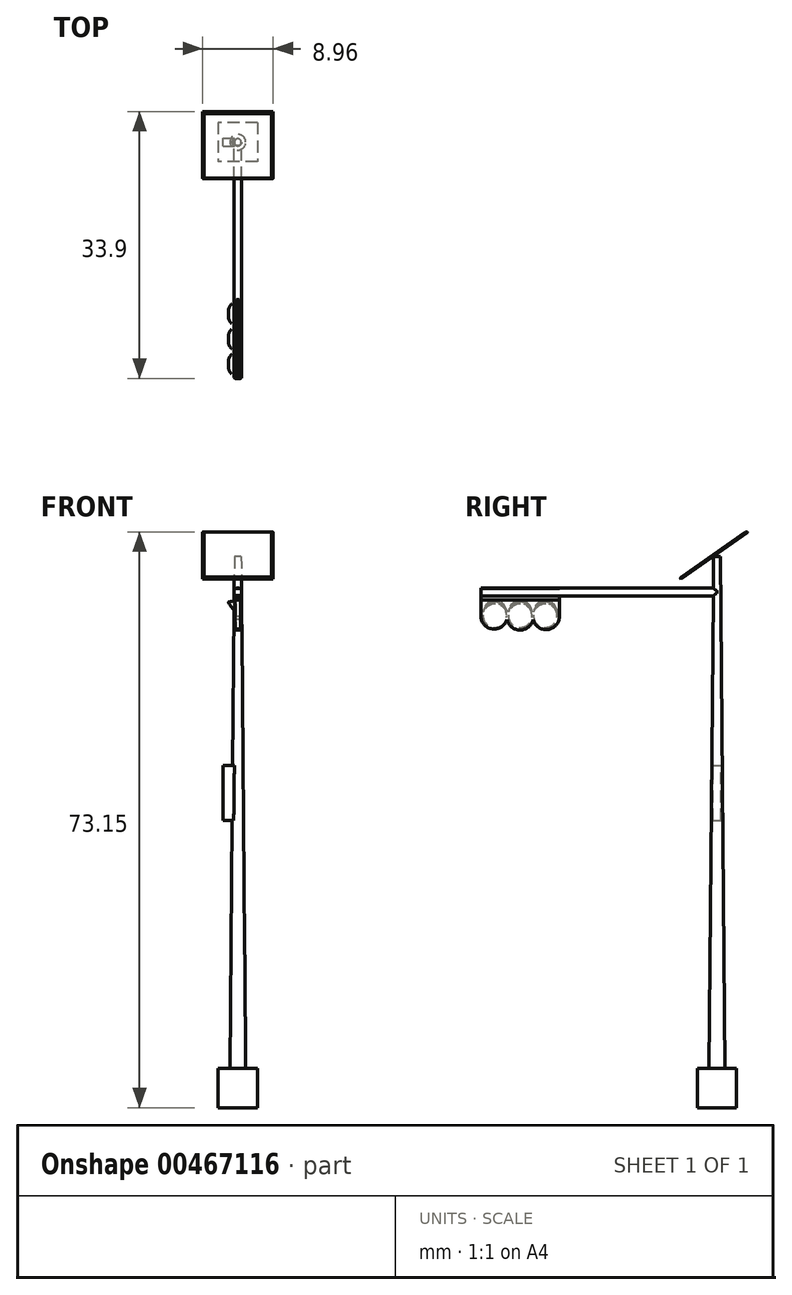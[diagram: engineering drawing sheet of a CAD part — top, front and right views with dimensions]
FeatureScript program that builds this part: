
annotation { "Feature Type Name" : "Feature", "Feature Type Description" : "" }
export const myFeature = defineFeature(function(context is Context, id is Id, definition is map)
    precondition{}
    {
        {
            var Q0;
            Q0=qCreatedBy(makeId("Top.planeOp"),FACE);
            var sketch = newSketch(context, id + "F0", { "sketchPlane" : qUnion([Q0])});
            skLineSegment(sketch, "E0.bottom", {"start": v(2.5, 2.5) * mm, "end": v(-2.5, 2.5) * mm});
            skLineSegment(sketch, "E0.top", {"start": v(2.5, -2.5) * mm, "end": v(-2.5, -2.5) * mm});
            skLineSegment(sketch, "E0.left", {"start": v(2.5, 2.5) * mm, "end": v(2.5, -2.5) * mm});
            skLineSegment(sketch, "E0.right", {"start": v(-2.5, 2.5) * mm, "end": v(-2.5, -2.5) * mm});
            skPoint(sketch, "E0.middle", {"position": v(0, 0) * mm});
            skSolve(sketch);
        }
        {
            var Q0;
            Q0 = qSketchRegion(id + "F0", true);
            extrude(context, id + "F1", {"entities" : qUnion([Q0]), "depth" : 5 * mm});
        }
        {
            var Q0;
            Q0=makeQuery(id+"F1.opExtrude","CAP_FACE",FACE,{"disambiguationData":[OSD([sQuery(id+"F0.wireOp",EDGE,"E0.bottom"),sQuery(id+"F0.wireOp",EDGE,"E0.top"),sQuery(id+"F0.wireOp",EDGE,"E0.left"),sQuery(id+"F0.wireOp",EDGE,"E0.right")])],"isStart":false});
            var sketch = newSketch(context, id + "F2", { "sketchPlane" : qUnion([Q0])});
            skCircle(sketch, "E1", {"center": v(0, 0) * mm, "radius": 1 * mm});
            skSolve(sketch);
        }
        {
            var Q0;
            Q0 = qSketchRegion(id + "F2", true);
            extrude(context, id + "F3", {"entities" : qUnion([Q0]), "operationType" : NewBodyOperationType.ADD, "depth" : 65 * mm, "hasDraft" : true, "draftAngle" : 0.5 * degree, "draftPullDirection" : true});
        }
        {
            var Q0;
            Q0=makeQuery(id+"F1.opExtrude","SWEPT_FACE",FACE,{"disambiguationData":[OSD([sQuery(id+"F0.wireOp",EDGE,"E0.left")])]});
            cPlane(context, id + "F4", {"entities" : qUnion([Q0]), "cplaneType" : CPlaneType.OFFSET, "offset" : 2.5 * mm, "oppositeDirection" : true, "width" : 150 * mm, "height" : 150 * mm});
        }
        {
            var Q0;
            Q0=qCreatedBy(id+"F4.planeOp",FACE);
            var sketch = newSketch(context, id + "F5", { "sketchPlane" : qUnion([Q0])});
            skLineSegment(sketch, "E2", {"start": v(-3.33, 68) * mm, "end": v(2.66, 72.2) * mm, "construction": true});
            skLineSegment(sketch, "E3.0", {"start": v(-0.43, 70) * mm, "end": v(0.43, 70) * mm, "construction": true});
            skSolve(sketch);
        }
        {
            var Q0;
            Q0=sQuery(id+"F5.wireOp",EDGE,"E2");
            cPlane(context, id + "F6", {"entities" : qUnion([Q0]), "cplaneType" : CPlaneType.LINE_ANGLE, "offset" : 25 * mm, "angle" : 0 * degree, "width" : 150 * mm, "height" : 150 * mm});
        }
        {
            var Q0;
            Q0=makeQuery(id+"F1.opExtrude","SWEPT_FACE",FACE,{"disambiguationData":[OSD([sQuery(id+"F0.wireOp",EDGE,"E0.top")])]});
            cPlane(context, id + "F7", {"entities" : qUnion([Q0]), "cplaneType" : CPlaneType.OFFSET, "offset" : 2.5 * mm, "oppositeDirection" : true, "width" : 150 * mm, "height" : 150 * mm});
        }
        {
            var Q0;
            Q0=qCreatedBy(id+"F7.planeOp",FACE);
            var sketch = newSketch(context, id + "F8", { "sketchPlane" : qUnion([Q0])});
            skLineSegment(sketch, "E4.0", {"start": v(0, 65) * mm, "end": v(0, 72.2) * mm, "construction": true});
            skCircle(sketch, "E5", {"center": v(0, 65.5) * mm, "radius": 0.5 * mm});
            skSolve(sketch);
        }
        {
            var Q0;
            Q0 = qSketchRegion(id + "F8", true);
            extrude(context, id + "F9", {"entities" : qUnion([Q0]), "operationType" : NewBodyOperationType.ADD, "depth" : 30 * mm});
        }
        {
            var Q0;
            Q0=qCreatedBy(id+"F6.planeOp",FACE);
            var sketch = newSketch(context, id + "F10", { "sketchPlane" : qUnion([Q0])});
            skLineSegment(sketch, "E6.0", {"start": v(0, 36.27) * mm, "end": v(0, 43.59) * mm, "construction": true});
            skLineSegment(sketch, "E7.bottom", {"start": v(4.48, 34.76) * mm, "end": v(-4.48, 34.76) * mm});
            skLineSegment(sketch, "E7.top", {"start": v(4.48, 45.1) * mm, "end": v(-4.48, 45.1) * mm});
            skLineSegment(sketch, "E7.left", {"start": v(4.48, 34.76) * mm, "end": v(4.48, 45.1) * mm});
            skLineSegment(sketch, "E7.right", {"start": v(-4.48, 34.76) * mm, "end": v(-4.48, 45.1) * mm});
            skPoint(sketch, "E7.middle", {"position": v(0, 39.93) * mm});
            skSolve(sketch);
        }
        {
            var Q0;
            Q0 = qSketchRegion(id + "F10", true);
            extrude(context, id + "F11", {"entities" : qUnion([Q0]), "depth" : .2 * mm});
        }
        {
            var Q0;
            Q0=makeQuery(id+"F11.opExtrude","CAP_FACE",FACE,{"disambiguationData":[OSD([sQuery(id+"F10.wireOp",EDGE,"E7.bottom"),sQuery(id+"F10.wireOp",EDGE,"E7.top"),sQuery(id+"F10.wireOp",EDGE,"E7.left"),sQuery(id+"F10.wireOp",EDGE,"E7.right")])],"isStart":false});
            fillet(context, id + "F12", {"entities" : qUnion([Q0]), "radius" : .2 * mm, "tangentPropagation" : true, "allowEdgeOverflow" : false});
        }
        {
            var Q0;
            Q0=qCreatedBy(id+"F4.planeOp",FACE);
            var sketch = newSketch(context, id + "F13", { "sketchPlane" : qUnion([Q0])});
            skLineSegment(sketch, "E8", {"start": v(-0.48, 65) * mm, "end": v(-20, 65) * mm, "construction": true});
            skLineSegment(sketch, "E9", {"start": v(-1, 5) * mm, "end": v(-0.43, 70) * mm, "construction": true});
            skLineSegment(sketch, "E10.top", {"start": v(-30, 64.5) * mm, "end": v(-20, 64.5) * mm});
            skLineSegment(sketch, "E10.left", {"start": v(-30, 66) * mm, "end": v(-30, 64.5) * mm});
            skLineSegment(sketch, "E10.right", {"start": v(-20, 66) * mm, "end": v(-20, 64.5) * mm});
            skLineSegment(sketch, "E11", {"start": v(-30, 66) * mm, "end": v(-0.47, 66) * mm});
            skLineSegment(sketch, "E12.0", {"start": v(-30, 65) * mm, "end": v(-30, 66) * mm});
            skSolve(sketch);
        }
        {
            var Q0;
            Q0 = qSketchRegion(id + "F13", true);
            extrude(context, id + "F14", {"entities" : qUnion([Q0]), "operationType" : NewBodyOperationType.ADD, "endBound" : BoundingType.SYMMETRIC, "depth" : 0.3 * mm});
        }
        {
            var Q0;
            Q0=qCreatedBy(id+"F4.planeOp",FACE);
            var sketch = newSketch(context, id + "F15", { "sketchPlane" : qUnion([Q0])});
            skLineSegment(sketch, "E13.0", {"start": v(-30, 64.5) * mm, "end": v(-30, 64.5) * mm});
            skLineSegment(sketch, "E14.0", {"start": v(-30, 64.5) * mm, "end": v(-20, 64.5) * mm});
            skLineSegment(sketch, "E15.top", {"start": v(-30, 60.5) * mm, "end": v(-20, 60.5) * mm});
            skLineSegment(sketch, "E15.left", {"start": v(-30, 64.5) * mm, "end": v(-30, 60.5) * mm});
            skLineSegment(sketch, "E15.right", {"start": v(-20, 64.5) * mm, "end": v(-20, 60.5) * mm});
            skLineSegment(sketch, "E16", {"start": v(-20, 62.5) * mm, "end": v(-30, 62.5) * mm, "construction": true});
            skCircle(sketch, "E17", {"center": v(-25, 62.5) * mm, "radius": 1.5 * mm});
            skCircle(sketch, "E18", {"center": v(-28.2, 62.5) * mm, "radius": 1.5 * mm});
            skCircle(sketch, "E19", {"center": v(-21.8, 62.5) * mm, "radius": 1.5 * mm});
            skArc(sketch, "E20", {"start": v(-20.3, 62.5) * mm, "mid": v(-21.8, 64.5) * mm, "end": v(-23.3, 62.5) * mm});
            skArc(sketch, "E21", {"start": v(-23.5, 62.5) * mm, "mid": v(-25, 64.5) * mm, "end": v(-26.5, 62.5) * mm});
            skArc(sketch, "E22", {"start": v(-26.7, 62.5) * mm, "mid": v(-28.2, 64.5) * mm, "end": v(-29.7, 62.5) * mm});
            skSolve(sketch);
        }
        {
            var Q0;
            Q0=makeQuery(id+"F15.imprint","IMPRINT",FACE,{"disambiguationData":[TD([[makeQuery(id+"F15.imprint","IMPRINT",EDGE,{"derivedFrom":sQuery(id+"F15.wireOp",EDGE,"E14.0")}),-1.0]])]});
            var Q1;
            {var subQ0=sQuery(id+"F15.wireOp",EDGE,"E22");var subQ1=sQuery(id+"F15.wireOp",EDGE,"E18");var subQ2=makeQuery(id+"F15.imprint","INTERSECT",VERTEX,{"disambiguationData":[OD(0.0)],"derivedFrom":[subQ1,subQ0]});Q1=makeQuery(id+"F15.imprint","IMPRINT",FACE,{"disambiguationData":[TD([[makeQuery(id+"F15.imprint","IMPRINT",EDGE,{"disambiguationData":[TD([[subQ2,-1.0]])],"derivedFrom":subQ1}),1.0]])]});}
            var Q2;
            {var subQ0=sQuery(id+"F15.wireOp",EDGE,"E22");Q2=makeQuery(id+"F15.imprint","IMPRINT",FACE,{"disambiguationData":[TD([[makeQuery(id+"F15.imprint","IMPRINT",EDGE,{"derivedFrom":subQ0}),1.0]])]});}
            var Q3;
            {var subQ0=sQuery(id+"F15.wireOp",EDGE,"E21");Q3=makeQuery(id+"F15.imprint","IMPRINT",FACE,{"disambiguationData":[TD([[makeQuery(id+"F15.imprint","IMPRINT",EDGE,{"derivedFrom":subQ0}),1.0]])]});}
            var Q4;
            {var subQ0=sQuery(id+"F15.wireOp",EDGE,"E20");Q4=makeQuery(id+"F15.imprint","IMPRINT",FACE,{"disambiguationData":[TD([[makeQuery(id+"F15.imprint","IMPRINT",EDGE,{"derivedFrom":subQ0}),1.0]])]});}
            var Q5;
            {var subQ0=sQuery(id+"F15.wireOp",EDGE,"E21");var subQ1=sQuery(id+"F15.wireOp",EDGE,"E17");var subQ2=makeQuery(id+"F15.imprint","INTERSECT",VERTEX,{"disambiguationData":[OD(0.0)],"derivedFrom":[subQ1,subQ0]});Q5=makeQuery(id+"F15.imprint","IMPRINT",FACE,{"disambiguationData":[TD([[makeQuery(id+"F15.imprint","IMPRINT",EDGE,{"disambiguationData":[TD([[subQ2,-1.0]])],"derivedFrom":subQ1}),1.0]])]});}
            var Q6;
            {var subQ0=sQuery(id+"F15.wireOp",EDGE,"E20");var subQ1=sQuery(id+"F15.wireOp",EDGE,"E19");var subQ2=makeQuery(id+"F15.imprint","INTERSECT",VERTEX,{"disambiguationData":[OD(0.0)],"derivedFrom":[subQ1,subQ0]});Q6=makeQuery(id+"F15.imprint","IMPRINT",FACE,{"disambiguationData":[TD([[makeQuery(id+"F15.imprint","IMPRINT",EDGE,{"disambiguationData":[TD([[subQ2,-1.0]])],"derivedFrom":subQ1}),1.0]])]});}
            var Q7;
            Q7=sQuery(id+"F15.wireOp",EDGE,"E15.right");
            var Q8;
            Q8=sQuery(id+"F15.wireOp",EDGE,"E15.top");
            var Q9;
            Q9=sQuery(id+"F13.wireOp",EDGE,"E10.top");
            var Q10;
            Q10=sQuery(id+"F15.wireOp",EDGE,"E15.left");
            extrude(context, id + "F16", {"entities" : qUnion([Q0, Q1, Q2, Q3, Q4, Q5, Q6]), "surfaceEntities" : qUnion([Q7, Q8, Q9, Q10]), "endBound" : BoundingType.SYMMETRIC, "depth" : 0.7 * mm});
        }
        {
            var Q0;
            {var subQ0=sQuery(id+"F15.wireOp",EDGE,"E21");Q0=makeQuery(id+"F15.imprint","IMPRINT",FACE,{"disambiguationData":[TD([[makeQuery(id+"F15.imprint","IMPRINT",EDGE,{"derivedFrom":subQ0}),1.0]])]});}
            var Q1;
            {var subQ0=sQuery(id+"F15.wireOp",EDGE,"E20");Q1=makeQuery(id+"F15.imprint","IMPRINT",FACE,{"disambiguationData":[TD([[makeQuery(id+"F15.imprint","IMPRINT",EDGE,{"derivedFrom":subQ0}),1.0]])]});}
            var Q2;
            {var subQ0=sQuery(id+"F15.wireOp",EDGE,"E22");Q2=makeQuery(id+"F15.imprint","IMPRINT",FACE,{"disambiguationData":[TD([[makeQuery(id+"F15.imprint","IMPRINT",EDGE,{"derivedFrom":subQ0}),1.0]])]});}
            extrude(context, id + "F17", {"entities" : qUnion([Q0, Q1, Q2]), "operationType" : NewBodyOperationType.ADD, "oppositeDirection" : true, "depth" : 1.16 * mm, "hasDraft" : true, "draftAngle" : 11 * degree, "draftPullDirection" : true});
        }
        {
            var Q0;
            Q0=makeQuery(id+"F16.opExtrude","SWEPT_EDGE",EDGE,{"disambiguationData":[OSD([sQuery(id+"F15.wireOp",EDGE,"E15.top"),sQuery(id+"F15.wireOp",EDGE,"E15.right")])]});
            var Q1;
            Q1=makeQuery(id+"F16.opExtrude","SWEPT_EDGE",EDGE,{"disambiguationData":[OSD([sQuery(id+"F15.wireOp",EDGE,"E15.top"),sQuery(id+"F15.wireOp",EDGE,"E15.left")])]});
            fillet(context, id + "F18", {"entities" : qUnion([Q0, Q1]), "radius" : 1.79 * mm, "tangentPropagation" : true, "allowEdgeOverflow" : false});
        }
        {
            var Q0;
            Q0=makeQuery(id+"F9.opExtrude","CAP_EDGE",EDGE,{"disambiguationData":[OSD([sQuery(id+"F8.wireOp",EDGE,"E5")])],"isStart":false});
            fillet(context, id + "F19", {"entities" : qUnion([Q0]), "radius" : .2 * mm, "tangentPropagation" : true, "allowEdgeOverflow" : false});
        }
        {
            var Q0;
            Q0=makeQuery(id+"F16.opExtrude","CAP_FACE",FACE,{"disambiguationData":[OSD([sQuery(id+"F15.wireOp",EDGE,"E14.0"),sQuery(id+"F15.wireOp",EDGE,"E15.top"),sQuery(id+"F15.wireOp",EDGE,"E15.left"),sQuery(id+"F15.wireOp",EDGE,"E15.right")])],"isStart":true});
            var sketch = newSketch(context, id + "F20", { "sketchPlane" : qUnion([Q0])});
            skArc(sketch, "E23", {"start": v(20, 62.48) * mm, "mid": v(21.47, 60.75) * mm, "end": v(23.35, 62.02) * mm});
            skArc(sketch, "E24", {"start": v(23.35, 62.02) * mm, "mid": v(25, 60.68) * mm, "end": v(26.67, 62.02) * mm});
            skPoint(sketch, "E25.orphan", {"position": v(26.5, 62.21) * mm});
            skArc(sketch, "E26", {"start": v(26.67, 62.02) * mm, "mid": v(28.54, 60.82) * mm, "end": v(30, 62.5) * mm});
            skArc(sketch, "E27.0", {"start": v(20, 62.29) * mm, "mid": v(20.52, 61.02) * mm, "end": v(21.79, 60.5) * mm});
            skLineSegment(sketch, "E28.0", {"start": v(30, 60.5) * mm, "end": v(20, 60.5) * mm});
            skArc(sketch, "E29.0", {"start": v(28.21, 60.5) * mm, "mid": v(29.48, 61.02) * mm, "end": v(30, 62.29) * mm});
            skLineSegment(sketch, "E30", {"start": v(30, 62.5) * mm, "end": v(30, 62.29) * mm});
            skLineSegment(sketch, "E31", {"start": v(20, 62.48) * mm, "end": v(20, 62.29) * mm});
            skSolve(sketch);
        }
        {
            var Q0;
            Q0 = qSketchRegion(id + "F20", true);
            extrude(context, id + "F21", {"entities" : qUnion([Q0]), "operationType" : NewBodyOperationType.REMOVE, "endBound" : BoundingType.SYMMETRIC, "oppositeDirection" : true, "depth" : 300 * mm});
        }
        {
            var Q0;
            Q0=makeQuery(id+"F16.opExtrude","CAP_FACE",FACE,{"disambiguationData":[OSD([sQuery(id+"F15.wireOp",EDGE,"E14.0"),sQuery(id+"F15.wireOp",EDGE,"E15.top"),sQuery(id+"F15.wireOp",EDGE,"E15.left"),sQuery(id+"F15.wireOp",EDGE,"E15.right")])],"isStart":true});
            var sketch = newSketch(context, id + "F22", { "sketchPlane" : qUnion([Q0])});
            skCircle(sketch, "E32.0", {"center": v(21.8, 62.5) * mm, "radius": 1.5 * mm});
            skCircle(sketch, "E33.0", {"center": v(25, 62.5) * mm, "radius": 1.5 * mm});
            skCircle(sketch, "E34.0", {"center": v(28.2, 62.5) * mm, "radius": 1.5 * mm});
            skSolve(sketch);
        }
        {
            var Q0;
            Q0 = qSketchRegion(id + "F22", true);
            extrude(context, id + "F23", {"entities" : qUnion([Q0]), "endBound" : BoundingType.SYMMETRIC, "depth" : .22 * mm});
        }
        {
            var Q0;
            Q0=qCreatedBy(id+"F4.planeOp",FACE);
            var sketch = newSketch(context, id + "F24", { "sketchPlane" : qUnion([Q0])});
            skLineSegment(sketch, "E35", {"start": v(0, 0) * mm, "end": v(0, 69.95) * mm, "construction": true});
            skPoint(sketch, "E36.middle", {"position": v(0, 36.33) * mm});
            skSolve(sketch);
        }
        {
            var Q0;
            Q0=makeQuery(id+"F1.opExtrude","SWEPT_FACE",FACE,{"disambiguationData":[OSD([sQuery(id+"F0.wireOp",EDGE,"E0.right")])]});
            cPlane(context, id + "F25", {"entities" : qUnion([Q0]), "cplaneType" : CPlaneType.OFFSET, "offset" : 1.63 * mm, "oppositeDirection" : true, "width" : 150 * mm, "height" : 150 * mm});
        }
        {
            var Q0;
            Q0=qCreatedBy(id+"F25.planeOp",FACE);
            var sketch = newSketch(context, id + "F26", { "sketchPlane" : qUnion([Q0])});
            skLineSegment(sketch, "E37.0", {"start": v(0, 0) * mm, "end": v(0, 69.95) * mm, "construction": true});
            skLineSegment(sketch, "E38.bottom", {"start": v(0.5, 36.5) * mm, "end": v(-0.5, 36.5) * mm});
            skLineSegment(sketch, "E38.top", {"start": v(0.5, 43.5) * mm, "end": v(-0.5, 43.5) * mm});
            skLineSegment(sketch, "E38.left", {"start": v(0.5, 36.5) * mm, "end": v(0.5, 43.5) * mm});
            skLineSegment(sketch, "E38.right", {"start": v(-0.5, 36.5) * mm, "end": v(-0.5, 43.5) * mm});
            skPoint(sketch, "E38.middle", {"position": v(0, 40) * mm});
            skSolve(sketch);
        }
        {
            var Q0;
            Q0 = qSketchRegion(id + "F26", true);
            extrude(context, id + "F27", {"entities" : qUnion([Q0]), "operationType" : NewBodyOperationType.ADD, "endBound" : BoundingType.SYMMETRIC, "depth" : 2 * mm});
        }
        {
            var Q0;
            Q0=makeQuery(id+"F11.opExtrude","CAP_FACE",FACE,{"disambiguationData":[OSD([sQuery(id+"F10.wireOp",EDGE,"E7.bottom"),sQuery(id+"F10.wireOp",EDGE,"E7.top"),sQuery(id+"F10.wireOp",EDGE,"E7.left"),sQuery(id+"F10.wireOp",EDGE,"E7.right")])],"isStart":false});
            var sketch = newSketch(context, id + "F28", { "sketchPlane" : qUnion([Q0])});
            skLineSegment(sketch, "E39.0.0", {"start": v(4.28, 44.9) * mm, "end": v(-4.28, 44.9) * mm});
            skLineSegment(sketch, "E39.0.1", {"start": v(-4.28, 44.9) * mm, "end": v(-4.28, 34.96) * mm});
            skLineSegment(sketch, "E39.0.2", {"start": v(-4.28, 34.96) * mm, "end": v(4.28, 34.96) * mm});
            skLineSegment(sketch, "E39.0.3", {"start": v(4.28, 34.96) * mm, "end": v(4.28, 44.9) * mm});
            skSolve(sketch);
        }
        {
            var Q0;
            Q0 = qSketchRegion(id + "F28", true);
            extrude(context, id + "F29", {"entities" : qUnion([Q0]), "depth" : 0.02 * mm});
        }
    });
